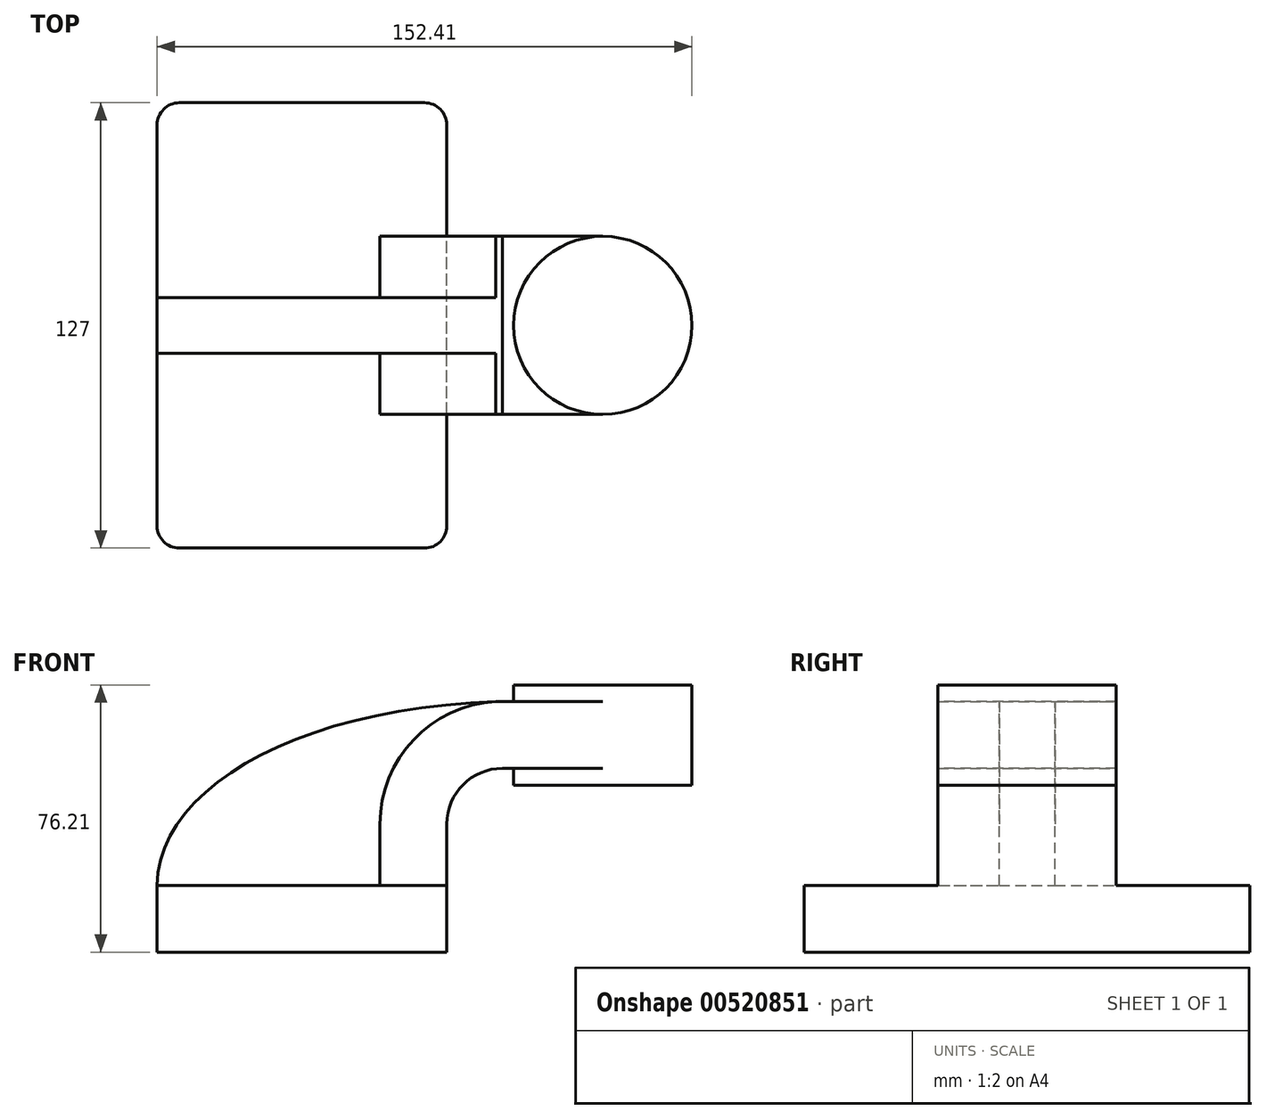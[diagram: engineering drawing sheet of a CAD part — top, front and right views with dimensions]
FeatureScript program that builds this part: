
annotation { "Feature Type Name" : "Feature", "Feature Type Description" : "" }
export const myFeature = defineFeature(function(context is Context, id is Id, definition is map)
    precondition{}
    {
        {
            var Q0;
            Q0=qCreatedBy(makeId("Front.planeOp"),FACE);
            var sketch = newSketch(context, id + "F0", { "sketchPlane" : qUnion([Q0])});
            skLineSegment(sketch, "E0.bottom", {"start": v(41.27, 9.53) * mm, "end": v(-41.28, 9.53) * mm});
            skLineSegment(sketch, "E0.top", {"start": v(41.28, -9.52) * mm, "end": v(-41.27, -9.52) * mm});
            skLineSegment(sketch, "E0.left", {"start": v(41.28, 9.53) * mm, "end": v(41.28, -9.52) * mm});
            skLineSegment(sketch, "E0.right", {"start": v(-41.28, 9.53) * mm, "end": v(-41.27, -9.52) * mm});
            skPoint(sketch, "E0.middle", {"position": v(0, 0) * mm});
            skLineSegment(sketch, "E1.bottom", {"start": v(111.12, 38.1) * mm, "end": v(60.32, 38.1) * mm});
            skLineSegment(sketch, "E1.top", {"start": v(111.12, 66.68) * mm, "end": v(60.32, 66.68) * mm});
            skLineSegment(sketch, "E1.left", {"start": v(111.12, 38.1) * mm, "end": v(111.12, 66.68) * mm});
            skLineSegment(sketch, "E1.right", {"start": v(60.32, 38.1) * mm, "end": v(60.32, 66.68) * mm});
            skPoint(sketch, "E1.middle", {"position": v(85.72, 52.39) * mm});
            skLineSegment(sketch, "E2", {"start": v(41.27, 9.53) * mm, "end": v(41.27, 27) * mm});
            skArc(sketch, "E3", {"start": v(41.27, 27) * mm, "mid": v(45.92, 38.23) * mm, "end": v(57.15, 42.88) * mm});
            skLineSegment(sketch, "E4", {"start": v(57.15, 42.88) * mm, "end": v(85.72, 42.88) * mm});
            skLineSegment(sketch, "E5.0", {"start": v(57.15, 61.93) * mm, "end": v(85.72, 61.93) * mm});
            skArc(sketch, "E5.1", {"start": v(22.23, 27) * mm, "mid": v(32.45, 51.7) * mm, "end": v(57.15, 61.93) * mm});
            skLineSegment(sketch, "E5.2", {"start": v(22.22, 9.53) * mm, "end": v(22.22, 27) * mm});
            skLineSegment(sketch, "E6", {"start": v(85.72, 61.93) * mm, "end": v(85.72, 42.88) * mm});
            skLineSegment(sketch, "E7", {"start": v(85.72, 61.93) * mm, "end": v(85.72, 66.68) * mm});
            skLineSegment(sketch, "E8", {"start": v(85.72, 66.68) * mm, "end": v(85.72, 38.1) * mm});
            skFitSpline(sketch, "E9", {"points": [v(-41.28, 9.53) * mm, v(57.15, 61.93) * mm], "startDerivative": vector(1.03, 84.46) * mm, "endDerivative": vector(171.45, 3.88) * mm});
            skPoint(sketch, "E10.1.internal.snap0", {"position": v(32.45, 51.7) * mm});
            skSolve(sketch);
        }
        {
            var Q0;
            Q0=makeQuery(id+"F0.imprint","IMPRINT",FACE,{"disambiguationData":[TD([[makeQuery(id+"F0.imprint","IMPRINT",EDGE,{"derivedFrom":sQuery(id+"F0.wireOp",EDGE,"E0.top")}),-1.0]])]});
            extrude(context, id + "F1", {"entities" : qUnion([Q0]), "endBound" : BoundingType.SYMMETRIC, "depth" : 127 * mm});
        }
        {
            var Q0;
            {var subQ1=sQuery(id+"F0.wireOp",EDGE,"E2");Q0=makeQuery(id+"F0.imprint","IMPRINT",FACE,{"disambiguationData":[TD([[makeQuery(id+"F0.imprint","IMPRINT",EDGE,{"derivedFrom":subQ1}),1.0]])]});}
            var Q1;
            {var subQ0=sQuery(id+"F0.wireOp",EDGE,"E4");var subQ1=sQuery(id+"F0.wireOp",EDGE,"E1.right");var subQ2=makeQuery(id+"F0.imprint","INTERSECT",VERTEX,{"derivedFrom":[subQ1,subQ0]});Q1=makeQuery(id+"F0.imprint","IMPRINT",FACE,{"disambiguationData":[TD([[makeQuery(id+"F0.imprint","IMPRINT",EDGE,{"disambiguationData":[TD([[subQ2,-1.0]])],"derivedFrom":subQ1}),-1.0]])]});}
            extrude(context, id + "F2", {"entities" : qUnion([Q0, Q1]), "operationType" : NewBodyOperationType.ADD, "endBound" : BoundingType.SYMMETRIC, "depth" : 50.8 * mm});
        }
        {
            var Q0;
            {var subQ3=sQuery(id+"F0.wireOp",EDGE,"E5.2");Q0=makeQuery(id+"F0.imprint","IMPRINT",FACE,{"disambiguationData":[TD([[makeQuery(id+"F0.imprint","IMPRINT",EDGE,{"derivedFrom":subQ3}),1.0]])]});}
            extrude(context, id + "F3", {"entities" : qUnion([Q0]), "operationType" : NewBodyOperationType.ADD, "endBound" : BoundingType.SYMMETRIC, "depth" : 15.88 * mm});
        }
        {
            var Q0;
            {var subQ0=sQuery(id+"F0.wireOp",EDGE,"E1.left");Q0=makeQuery(id+"F0.imprint","IMPRINT",FACE,{"disambiguationData":[TD([[makeQuery(id+"F0.imprint","IMPRINT",EDGE,{"derivedFrom":subQ0}),1.0]])]});}
            var Q1;
            Q1=sQuery(id+"F0.wireOp",EDGE,"E8");
            revolve(context, id + "F4", {"operationType" : NewBodyOperationType.ADD, "entities" : qUnion([Q0]), "axis" : qUnion([Q1]), "revolveType" : RevolveType.FULL});
        }
        {
            var Q0;
            Q0=makeQuery(id+"F1.opExtrude","CAP_EDGE",EDGE,{"disambiguationData":[OSD([sQuery(id+"F0.wireOp",EDGE,"E0.left")])],"isStart":false});
            var Q1;
            Q1=makeQuery(id+"F1.opExtrude","CAP_EDGE",EDGE,{"disambiguationData":[OSD([sQuery(id+"F0.wireOp",EDGE,"E0.right")])],"isStart":false});
            var Q2;
            Q2=makeQuery(id+"F1.opExtrude","CAP_EDGE",EDGE,{"disambiguationData":[OSD([sQuery(id+"F0.wireOp",EDGE,"E0.left")])],"isStart":true});
            var Q3;
            Q3=makeQuery(id+"F1.opExtrude","CAP_EDGE",EDGE,{"disambiguationData":[OSD([sQuery(id+"F0.wireOp",EDGE,"E0.right")])],"isStart":true});
            fillet(context, id + "F5", {"entities" : qUnion([Q0, Q1, Q2, Q3]), "radius" : 6.35 * mm, "tangentPropagation" : true, "allowEdgeOverflow" : false});
        }
    });
